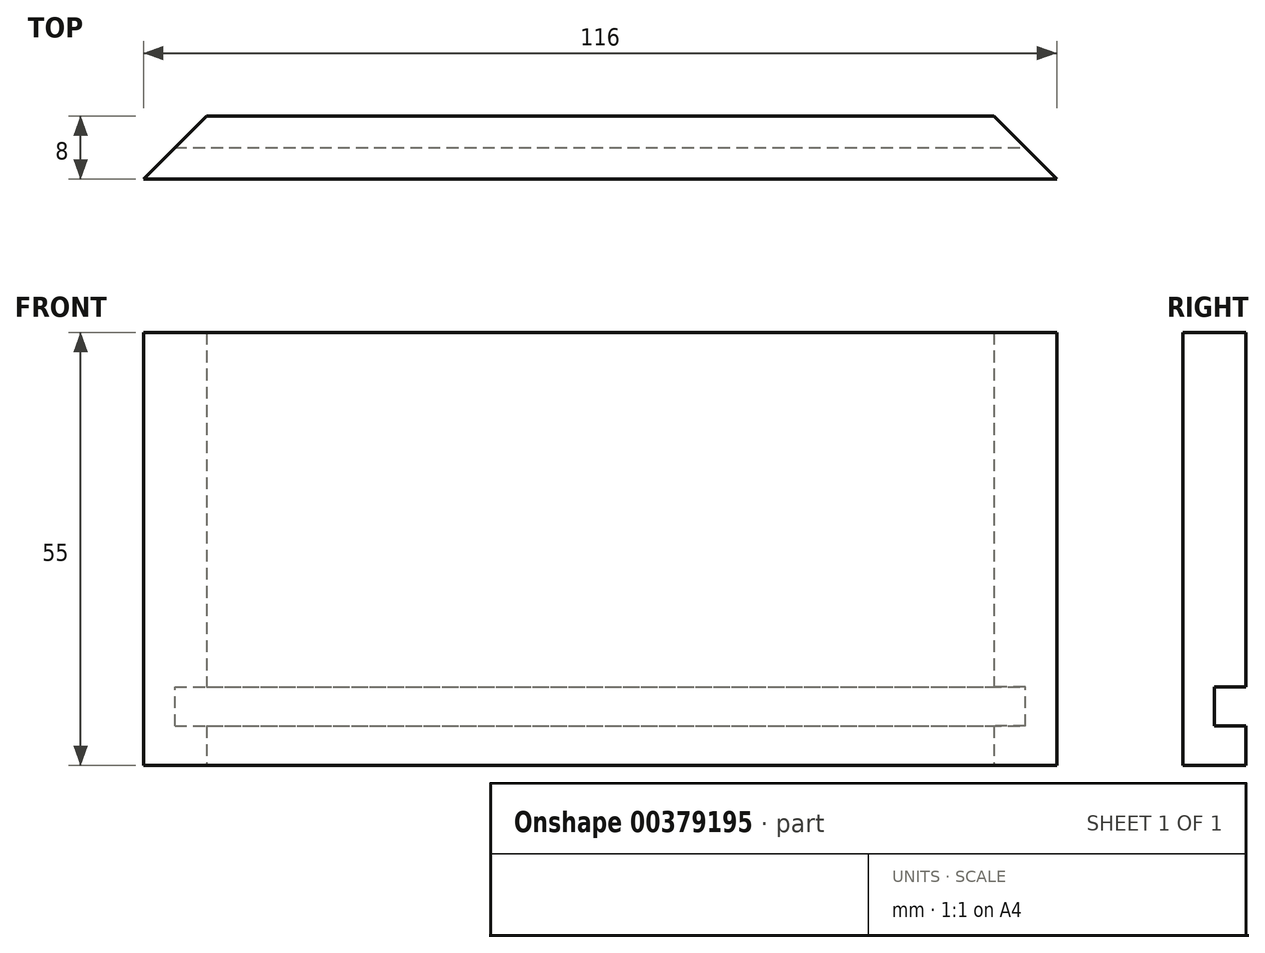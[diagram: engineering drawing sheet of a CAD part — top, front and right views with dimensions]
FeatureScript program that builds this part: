
annotation { "Feature Type Name" : "Feature", "Feature Type Description" : "" }
export const myFeature = defineFeature(function(context is Context, id is Id, definition is map)
    precondition{}
    {
        {
            var Q0;
            Q0=qCreatedBy(makeId("Top.planeOp"),FACE);
            var sketch = newSketch(context, id + "F0", { "sketchPlane" : qUnion([Q0])});
            skLineSegment(sketch, "E0.bottom", {"start": v(-58, -4) * mm, "end": v(58, -4) * mm});
            skLineSegment(sketch, "E1", {"start": v(-50, 4) * mm, "end": v(-58, -4) * mm});
            skLineSegment(sketch, "E2", {"start": v(50, 4) * mm, "end": v(58, -4) * mm});
            skLineSegment(sketch, "E3", {"start": v(-50, 4) * mm, "end": v(50, 4) * mm});
            skSolve(sketch);
        }
        {
            var Q0;
            Q0=makeQuery(id+"F0.imprint","IMPRINT",FACE,{"disambiguationData":[TD([[makeQuery(id+"F0.imprint","IMPRINT",EDGE,{"derivedFrom":sQuery(id+"F0.wireOp",EDGE,"E0.bottom")}),1.0]])]});
            extrude(context, id + "F1", {"entities" : qUnion([Q0]), "depth" : 55 * mm});
        }
        {
            var Q0;
            Q0=qCreatedBy(makeId("Right.planeOp"),FACE);
            var sketch = newSketch(context, id + "F2", { "sketchPlane" : qUnion([Q0])});
            skLineSegment(sketch, "E4.bottom", {"start": v(0, 5) * mm, "end": v(4, 5) * mm});
            skLineSegment(sketch, "E4.top", {"start": v(0, 10) * mm, "end": v(4, 10) * mm});
            skLineSegment(sketch, "E4.left", {"start": v(0, 5) * mm, "end": v(0, 10) * mm});
            skLineSegment(sketch, "E4.right", {"start": v(4, 5) * mm, "end": v(4, 10) * mm});
            skSolve(sketch);
        }
        {
            var Q0;
            Q0 = qSketchRegion(id + "F2", true);
            extrude(context, id + "F3", {"entities" : qUnion([Q0]), "operationType" : NewBodyOperationType.REMOVE, "endBound" : BoundingType.SYMMETRIC, "oppositeDirection" : true, "depth" : 116 * mm});
        }
    });
